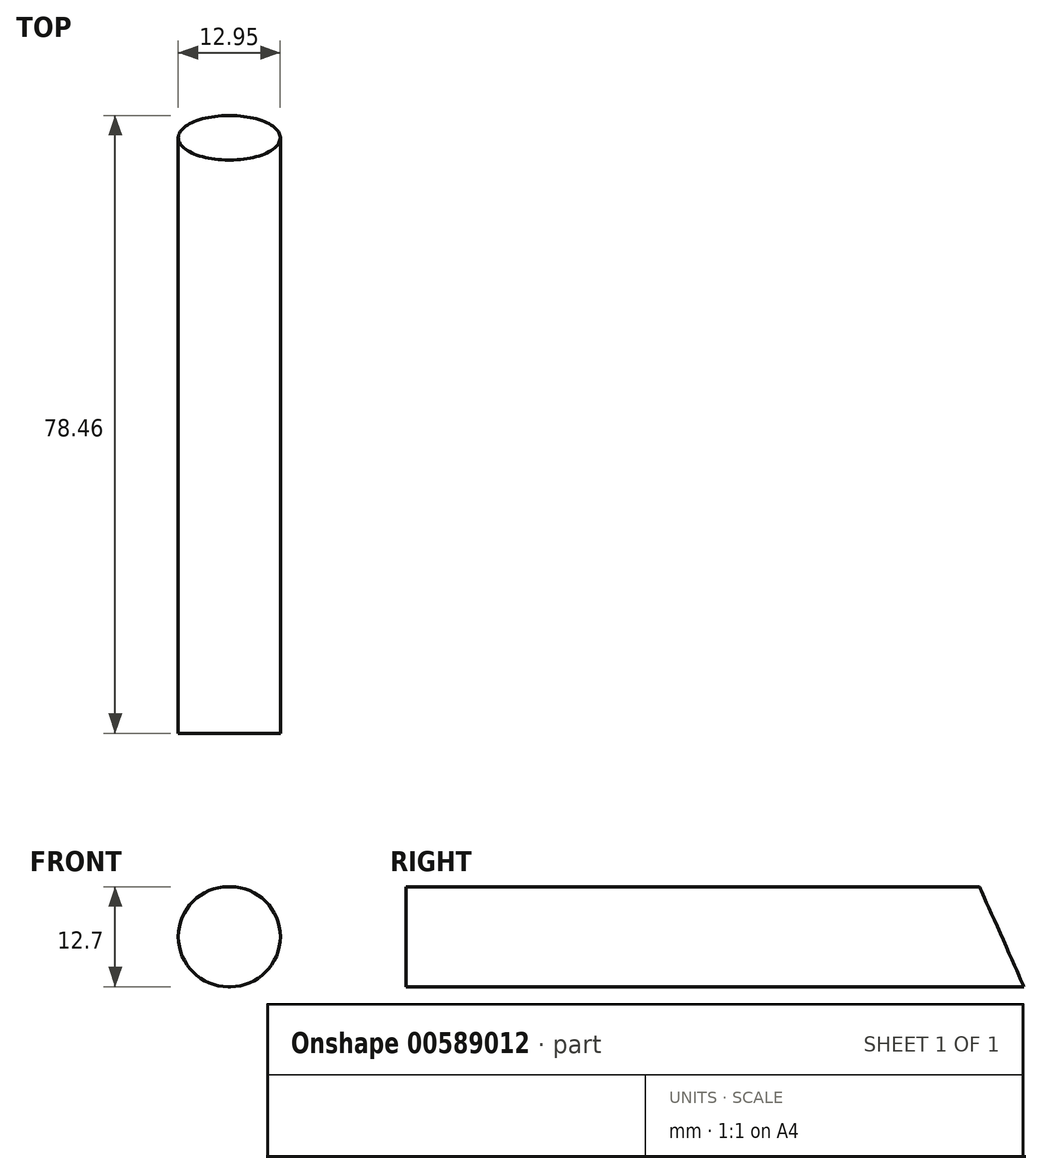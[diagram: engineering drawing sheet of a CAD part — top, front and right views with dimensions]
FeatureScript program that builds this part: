
annotation { "Feature Type Name" : "Feature", "Feature Type Description" : "" }
export const myFeature = defineFeature(function(context is Context, id is Id, definition is map)
    precondition{}
    {
        {
            var Q0;
            Q0=qCreatedBy(makeId("Front.planeOp"),FACE);
            var sketch = newSketch(context, id + "F0", { "sketchPlane" : qUnion([Q0])});
            skCircle(sketch, "E0", {"center": v(-1.63, 0) * mm, "radius": 9.53 * mm});
            skSolve(sketch);
        }
        {
            var Q0;
            Q0=qCreatedBy(makeId("Right.planeOp"),FACE);
            var sketch = newSketch(context, id + "F1", { "sketchPlane" : qUnion([Q0])});
            skLineSegment(sketch, "E1", {"start": v(-39.23, 0) * mm, "end": v(-39.23, 12.7) * mm});
            skLineSegment(sketch, "E2", {"start": v(-39.23, 12.7) * mm, "end": v(33.58, 12.7) * mm});
            skLineSegment(sketch, "E3", {"start": v(33.58, 12.7) * mm, "end": v(39.23, 0) * mm});
            skLineSegment(sketch, "E4", {"start": v(39.23, 0) * mm, "end": v(-39.23, 0) * mm});
            skSolve(sketch);
        }
        {
            var Q0;
            Q0 = qSketchRegion(id + "F1", true);
            extrude(context, id + "F2", {"entities" : qUnion([Q0]), "depth" : 12.95 * mm, "offsetDistance" : 25.4 * mm});
        }
        {
            var Q0;
            Q0=makeQuery(id+"F2.opExtrude","CAP_EDGE",EDGE,{"disambiguationData":[OSD([sQuery(id+"F1.wireOp",EDGE,"E4")])],"isStart":false});
            var Q1;
            Q1=makeQuery(id+"F2.opExtrude","CAP_EDGE",EDGE,{"disambiguationData":[OSD([sQuery(id+"F1.wireOp",EDGE,"E2")])],"isStart":false});
            var Q2;
            Q2=makeQuery(id+"F2.opExtrude","CAP_EDGE",EDGE,{"disambiguationData":[OSD([sQuery(id+"F1.wireOp",EDGE,"E2")])],"isStart":true});
            var Q3;
            Q3=makeQuery(id+"F2.opExtrude","CAP_EDGE",EDGE,{"disambiguationData":[OSD([sQuery(id+"F1.wireOp",EDGE,"E4")])],"isStart":true});
            fillet(context, id + "F3", {"entities" : qUnion([Q0, Q1, Q2, Q3]), "radius" : 6.35 * mm, "tangentPropagation" : true, "allowEdgeOverflow" : false});
        }
    });
